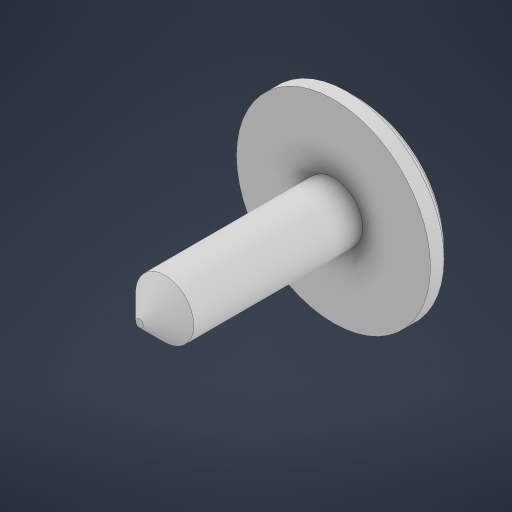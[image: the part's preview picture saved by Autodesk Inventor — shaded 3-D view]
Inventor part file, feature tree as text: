
AUTODESK INVENTOR PART (.ipt)
format: ipt  version: 2023 (Build 270158000, 158)  size: 269,824 bytes
history: native  units: mm
features: chamfer x5, extrude x3, sketch x3, fillet x1
ambient origin geometry x8: Origin, YZ Plane, XZ Plane, XY Plane, X Axis, Y Axis, Z Axis, Center Point
bodies: Solid1 (feature_tree)
feature tree (12):
  extrude  "Extrusion1"  Depth=2.0mm TaperAngle=0.0deg
  extrude  "Extrusion2"  Depth=10.0mm TaperAngle=0.0deg
  chamfer  "Chamfer1"  Distance=1.3mm Angle=45.0deg
  chamfer  "Chamfer2"  Distance=1.3mm Angle=45.0deg
  fillet  "Fillet1"  Radius=3.0mm
  extrude  "Extrusion3"  Depth=1.0mm
  chamfer  "Chamfer3"  Distance=1.0mm
  chamfer  "Chamfer4"  Distance=0.5mm Angle=45.0deg
  chamfer  "Chamfer5"  Distance=0.5mm Angle=45.0deg
  sketch  "Sketch1"  dims[d0=10.0mm d1=2.0mm d2=0.0mm]
  sketch  "Sketch2"  dims[d3=3.0mm d4=10.0mm d5=0.0mm d6=1.3mm d7=2.0mm d8=45.0deg d9=1.3mm d10=2.0mm d11=45.0deg d12=3.0mm]
  sketch  "Sketch3"  dims[d15=6.0mm d16=1.0mm d17=1.0mm d18=0.0mm d19=0.5mm d20=2.0mm d21=45.0deg d22=0.5mm d23=2.0mm d24=45.0deg d25=0.5mm d26=2.0mm d27=45.0deg]
